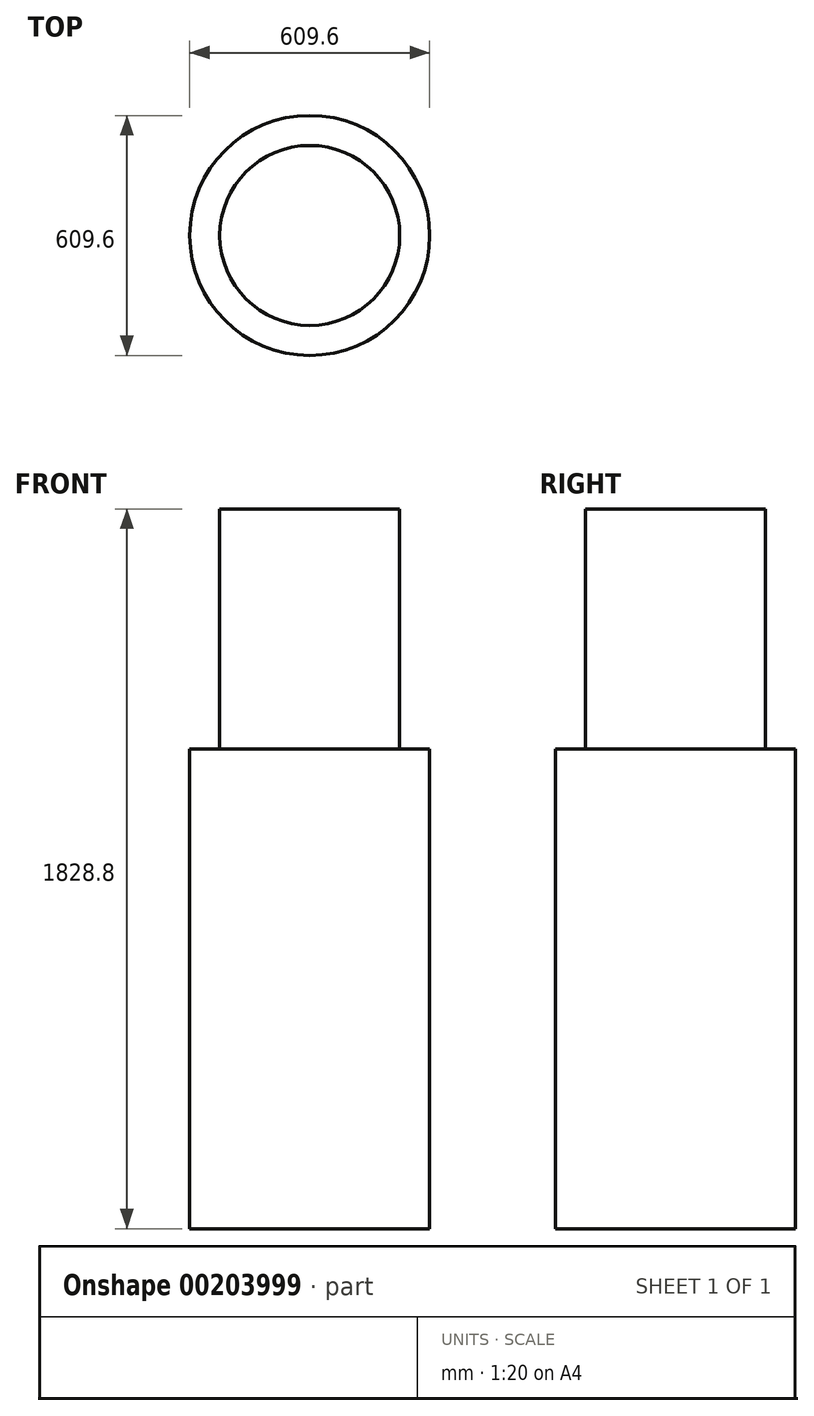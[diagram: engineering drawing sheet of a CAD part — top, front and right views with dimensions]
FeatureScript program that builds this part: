
annotation { "Feature Type Name" : "Feature", "Feature Type Description" : "" }
export const myFeature = defineFeature(function(context is Context, id is Id, definition is map)
    precondition{}
    {
        {
            var Q0;
            Q0=qCreatedBy(makeId("Front.planeOp"),FACE);
            var sketch = newSketch(context, id + "F0", { "sketchPlane" : qUnion([Q0])});
            skLineSegment(sketch, "E0", {"start": v(0, 0) * mm, "end": v(0, 1828.8) * mm});
            skLineSegment(sketch, "E1", {"start": v(0, 1828.8) * mm, "end": v(228.6, 1828.8) * mm});
            skLineSegment(sketch, "E2", {"start": v(228.6, 1828.8) * mm, "end": v(228.6, 1219.2) * mm});
            skLineSegment(sketch, "E3", {"start": v(228.6, 1219.2) * mm, "end": v(304.8, 1219.2) * mm});
            skLineSegment(sketch, "E4", {"start": v(304.8, 1219.2) * mm, "end": v(304.8, 0) * mm});
            skLineSegment(sketch, "E5", {"start": v(304.8, 0) * mm, "end": v(0, 0) * mm});
            skLineSegment(sketch, "E6", {"start": v(0, 1828.8) * mm, "end": v(0, 2060.47) * mm, "construction": true});
            skSolve(sketch);
        }
        {
            var Q0;
            Q0 = qSketchRegion(id + "F0", true);
            var Q1;
            Q1=sQuery(id+"F0.wireOp",EDGE,"E6");
            revolve(context, id + "F1", {"entities" : qUnion([Q0]), "axis" : qUnion([Q1]), "revolveType" : RevolveType.FULL});
        }
        {
            var Q0;
            Q0=makeQuery(id+"F1.opRevolve","SWEPT_FACE",FACE,{"disambiguationData":[OSD([sQuery(id+"F0.wireOp",EDGE,"E1")])]});
            cPlane(context, id + "F2", {"entities" : qUnion([Q0]), "cplaneType" : CPlaneType.OFFSET, "offset" : 50.8 * mm, "oppositeDirection" : true, "width" : 152.4 * mm, "height" : 152.4 * mm});
        }
        {
            var Q0;
            Q0=qCreatedBy(id+"F2.planeOp",FACE);
            var sketch = newSketch(context, id + "F3", { "sketchPlane" : qUnion([Q0])});
            skCircle(sketch, "E7.0", {"center": v(0, 0) * mm, "radius": 228.6 * mm, "construction": true});
            skCircle(sketch, "E8", {"center": v(0, 142.87) * mm, "radius": 6.35 * mm});
            skLineSegment(sketch, "E9", {"start": v(0, 142.87) * mm, "end": v(0, 0) * mm, "construction": true});
            skCircle(sketch, "E10.1.0", {"center": v(-123.73, 71.44) * mm, "radius": 6.35 * mm});
            skCircle(sketch, "E10.2.0", {"center": v(-123.73, -71.44) * mm, "radius": 6.35 * mm});
            skCircle(sketch, "E10.3.0", {"center": v(0, -142.87) * mm, "radius": 6.35 * mm});
            skCircle(sketch, "E10.4.0", {"center": v(123.73, -71.44) * mm, "radius": 6.35 * mm});
            skCircle(sketch, "E10.5.0", {"center": v(123.73, 71.44) * mm, "radius": 6.35 * mm});
            skSolve(sketch);
        }
        {
            var Q0;
            Q0 = qSketchRegion(id + "F3", true);
            var Q1;
            Q1=makeQuery(id+"F1.opRevolve","SWEPT_FACE",FACE,{"disambiguationData":[OSD([sQuery(id+"F0.wireOp",EDGE,"E5")])]});
            extrude(context, id + "F4", {"entities" : qUnion([Q0]), "endBound" : BoundingType.UP_TO_SURFACE, "oppositeDirection" : true, "endBoundEntityFace" : qUnion([Q1]), "depth" : 25.4 * mm});
        }
        {
            var Q0;
            Q0=qCreatedBy(makeId("Right.planeOp"),FACE);
            var sketch = newSketch(context, id + "F5", { "sketchPlane" : qUnion([Q0])});
            skLineSegment(sketch, "E11", {"start": v(149.22, 1778) * mm, "end": v(149.22, 0) * mm, "construction": true});
            skCircle(sketch, "E12", {"center": v(152.72, 1676.4) * mm, "radius": 4.76 * mm});
            skCircle(sketch, "E13.0.1.0", {"center": v(152.72, 1371.6) * mm, "radius": 4.76 * mm});
            skCircle(sketch, "E13.0.2.0", {"center": v(152.72, 1066.8) * mm, "radius": 4.76 * mm});
            skCircle(sketch, "E13.0.3.0", {"center": v(152.72, 762) * mm, "radius": 4.76 * mm});
            skCircle(sketch, "E13.0.4.0", {"center": v(152.72, 457.2) * mm, "radius": 4.76 * mm});
            skCircle(sketch, "E13.0.5.0", {"center": v(152.72, 152.4) * mm, "radius": 4.76 * mm});
            skLineSegment(sketch, "E13.direction1", {"start": v(152.72, 1676.4) * mm, "end": v(192.4, 1676.4) * mm, "construction": true});
            skLineSegment(sketch, "E13.direction2", {"start": v(152.72, 1676.4) * mm, "end": v(152.72, 1371.6) * mm, "construction": true});
            skLineSegment(sketch, "E14", {"start": v(0, 0) * mm, "end": v(0, 442.3) * mm, "construction": true});
            skSolve(sketch);
        }
        {
            var Q0;
            Q0 = qSketchRegion(id + "F5", true);
            var Q1;
            Q1=sQuery(id+"F5.wireOp",EDGE,"E14");
            revolve(context, id + "F6", {"operationType" : NewBodyOperationType.ADD, "entities" : qUnion([Q0]), "axis" : qUnion([Q1]), "revolveType" : RevolveType.FULL});
        }
    });
